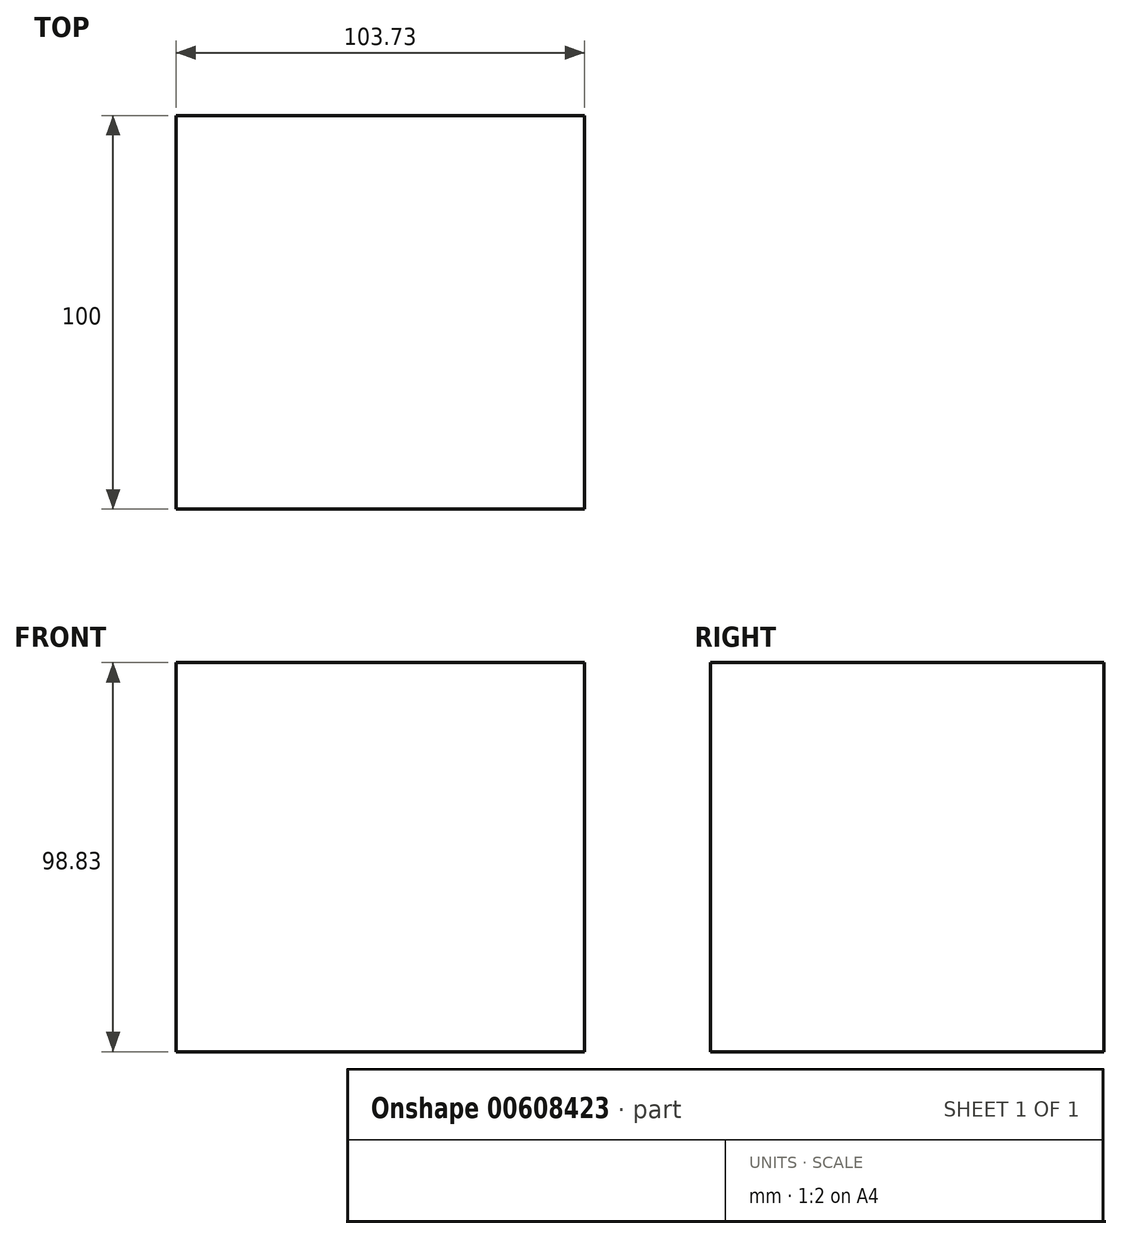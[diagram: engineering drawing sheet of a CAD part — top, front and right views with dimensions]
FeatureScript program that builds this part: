
annotation { "Feature Type Name" : "Feature", "Feature Type Description" : "" }
export const myFeature = defineFeature(function(context is Context, id is Id, definition is map)
    precondition{}
    {
        {
            var Q0;
            Q0=qCreatedBy(makeId("Front.planeOp"),FACE);
            var sketch = newSketch(context, id + "F0", { "sketchPlane" : qUnion([Q0])});
            skLineSegment(sketch, "E0.bottom", {"start": v(-48.5, -45.59) * mm, "end": v(55.23, -45.59) * mm});
            skLineSegment(sketch, "E0.top", {"start": v(-48.5, 53.24) * mm, "end": v(55.23, 53.24) * mm});
            skLineSegment(sketch, "E0.left", {"start": v(-48.5, -45.59) * mm, "end": v(-48.5, 53.24) * mm});
            skLineSegment(sketch, "E0.right", {"start": v(55.23, -45.59) * mm, "end": v(55.23, 53.24) * mm});
            skSolve(sketch);
        }
        {
            var Q0;
            Q0=makeQuery(id+"F0.imprint","IMPRINT",FACE,{"disambiguationData":[TD([[makeQuery(id+"F0.imprint","IMPRINT",EDGE,{"derivedFrom":sQuery(id+"F0.wireOp",EDGE,"E0.bottom")}),1.0]])]});
            extrude(context, id + "F1", {"entities" : qUnion([Q0]), "depth" : 100 * mm, "offsetDistance" : 25.4 * mm});
        }
    });
